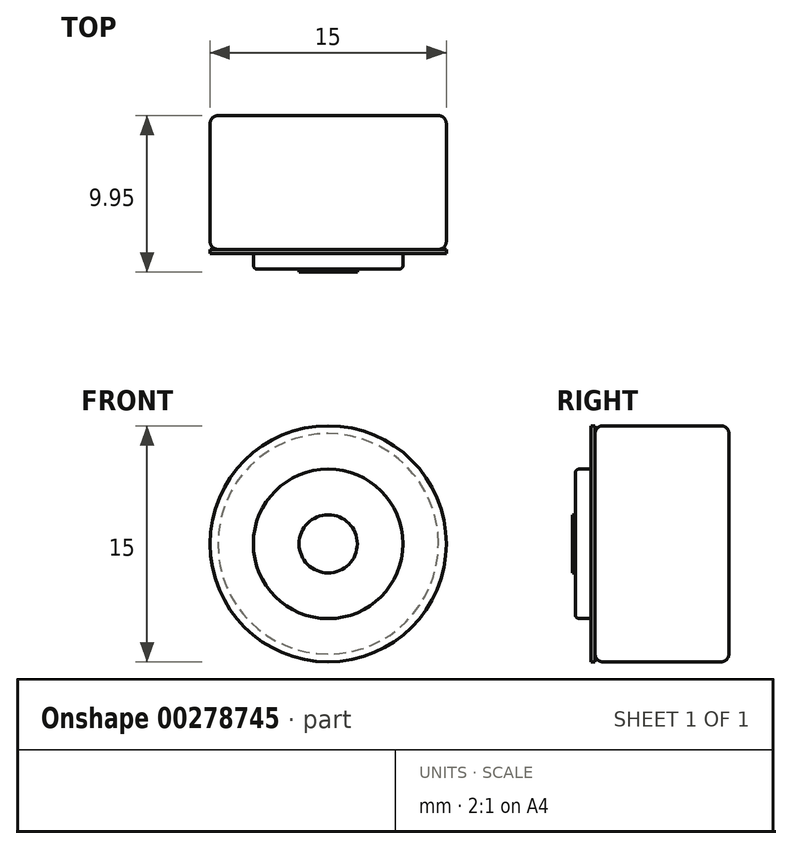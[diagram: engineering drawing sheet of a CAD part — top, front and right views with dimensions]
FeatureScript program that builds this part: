
annotation { "Feature Type Name" : "Feature", "Feature Type Description" : "" }
export const myFeature = defineFeature(function(context is Context, id is Id, definition is map)
    precondition{}
    {
        {
            var Q0;
            Q0=qCreatedBy(makeId("Front.planeOp"),FACE);
            var sketch = newSketch(context, id + "F0", { "sketchPlane" : qUnion([Q0])});
            skCircle(sketch, "E0", {"center": v(0, 0) * mm, "radius": 7.5 * mm});
            skSolve(sketch);
        }
        {
            var Q0;
            Q0=qSketchRegion(id+"F0",true);
            extrude(context, id + "F1", {"entities" : qUnion([Q0]), "depth" : 8.5 * mm});
        }
        {
            var Q0;
            Q0=makeQuery(id+"F1.opExtrude","CAP_EDGE",EDGE,{"disambiguationData":[OSD([sQuery(id+"F0.wireOp",EDGE,"E0")])],"isStart":false});
            var Q1;
            Q1=makeQuery(id+"F1.opExtrude","CAP_EDGE",EDGE,{"disambiguationData":[OSD([sQuery(id+"F0.wireOp",EDGE,"E0")])],"isStart":true});
            fillet(context, id + "F2", {"entities" : qUnion([Q0, Q1]), "radius" : 0.5 * mm, "tangentPropagation" : true, "allowEdgeOverflow" : false});
        }
        {
            var Q0;
            Q0=makeQuery(id+"F1.opExtrude","CAP_FACE",FACE,{"disambiguationData":[OSD([sQuery(id+"F0.wireOp",EDGE,"E0")])],"isStart":false});
            var sketch = newSketch(context, id + "F3", { "sketchPlane" : qUnion([Q0])});
            skCircle(sketch, "E1.0", {"center": v(0, 0) * mm, "radius": 7.5 * mm});
            skSolve(sketch);
        }
        {
            var Q0;
            Q0=qSketchRegion(id+"F3",true);
            extrude(context, id + "F4", {"entities" : qUnion([Q0]), "operationType" : NewBodyOperationType.ADD, "depth" : .25 * mm});
        }
        {
            var Q0;
            Q0=makeQuery(id+"F4.opExtrude","CAP_FACE",FACE,{"disambiguationData":[OSD([sQuery(id+"F3.wireOp",EDGE,"E1.0")])],"isStart":false});
            var sketch = newSketch(context, id + "F5", { "sketchPlane" : qUnion([Q0])});
            skCircle(sketch, "E2", {"center": v(0, 0) * mm, "radius": 4.75 * mm});
            skSolve(sketch);
        }
        {
            var Q0;
            Q0=qSketchRegion(id+"F5",true);
            extrude(context, id + "F6", {"entities" : qUnion([Q0]), "operationType" : NewBodyOperationType.ADD, "depth" : 1 * mm});
        }
        {
            var Q0;
            Q0=makeQuery(id+"F6.opExtrude","CAP_FACE",FACE,{"disambiguationData":[OSD([sQuery(id+"F5.wireOp",EDGE,"E2")])],"isStart":false});
            var sketch = newSketch(context, id + "F7", { "sketchPlane" : qUnion([Q0])});
            skCircle(sketch, "E3", {"center": v(0, 0) * mm, "radius": 1.85 * mm});
            skSolve(sketch);
        }
        {
            var Q0;
            Q0=qSketchRegion(id+"F7",true);
            extrude(context, id + "F8", {"entities" : qUnion([Q0]), "operationType" : NewBodyOperationType.ADD, "depth" : 0.2 * mm});
        }
        {
            var Q0;
            Q0=makeQuery(id+"F6.opExtrude","CAP_EDGE",EDGE,{"disambiguationData":[OSD([sQuery(id+"F5.wireOp",EDGE,"E2")])],"isStart":true});
            var Q1;
            Q1=makeQuery(id+"F6.opExtrude","CAP_EDGE",EDGE,{"disambiguationData":[OSD([sQuery(id+"F5.wireOp",EDGE,"E2")])],"isStart":false});
            fillet(context, id + "F9", {"entities" : qUnion([Q0, Q1]), "radius" : 0.25 * mm, "tangentPropagation" : true, "allowEdgeOverflow" : false});
        }
    });
